annotation { "Feature Type Name" : "Feature", "Feature Type Description" : "" }
export const myFeature = defineFeature(function(context is Context, id is Id, definition is map)
    precondition{}
    {
        {
            var Q0;
            Q0=qCreatedBy(makeId("Front.planeOp"),FACE);
            var sketch = newSketch(context, id + "F0", { "sketchPlane" : qUnion([Q0])});
            skLineSegment(sketch, "E0.bottom", {"start": v(-30.04, 68.09) * mm, "end": v(46.16, 68.09) * mm});
            skLineSegment(sketch, "E0.top", {"start": v(-30.04, -46.79) * mm, "end": v(46.16, -46.79) * mm});
            skLineSegment(sketch, "E0.left", {"start": v(-30.04, 68.09) * mm, "end": v(-30.04, -46.79) * mm});
            skLineSegment(sketch, "E0.right", {"start": v(46.16, 68.09) * mm, "end": v(46.16, -46.79) * mm});
            skSolve(sketch);
        }
        {
            var Q0;
            Q0 = qSketchRegion(id + "F0", true);
            extrude(context, id + "F1", {"entities" : qUnion([Q0]), "depth" : 3.17 * mm});
        }
        {
            var Q0;
            Q0=makeQuery(id+"F1.opExtrude","CAP_FACE",FACE,{"disambiguationData":[OSD([sQuery(id+"F0.wireOp",EDGE,"E0.bottom"),sQuery(id+"F0.wireOp",EDGE,"E0.top"),sQuery(id+"F0.wireOp",EDGE,"E0.left"),sQuery(id+"F0.wireOp",EDGE,"E0.right")])],"isStart":false});
            var sketch = newSketch(context, id + "F2", { "sketchPlane" : qUnion([Q0])});
            skText(sketch, "E1", { "text": "STEM Academy", "fontName": "OpenSans-Regular.ttf"});
            skText(sketch, "E2", { "text": "Hall Pass", "fontName": "OpenSans-Regular.ttf"});
            skLineSegment(sketch, "E3", {"start": v(-8.97, 21.63) * mm, "end": v(2.74, 15.23) * mm});
            skLineSegment(sketch, "E4", {"start": v(2.74, 15.23) * mm, "end": v(10.3, 29.05) * mm});
            skLineSegment(sketch, "E5", {"start": v(-8.97, 21.63) * mm, "end": v(-4.91, 29.05) * mm});
            skLineSegment(sketch, "E6", {"start": v(15.54, 33.96) * mm, "end": v(1.33, 33.96) * mm});
            skArc(sketch, "E7", {"start": v(1.33, 33.96) * mm, "mid": v(-2.64, 32.58) * mm, "end": v(-4.91, 29.05) * mm});
            skArc(sketch, "E8", {"start": v(15.54, 33.96) * mm, "mid": v(12.52, 31.92) * mm, "end": v(10.3, 29.05) * mm});
            skLineSegment(sketch, "E9", {"start": v(11.32, 16.01) * mm, "end": v(23.65, 16.01) * mm});
            skLineSegment(sketch, "E10", {"start": v(23.65, 16.01) * mm, "end": v(28.78, 25.39) * mm});
            skLineSegment(sketch, "E11", {"start": v(28.78, 25.39) * mm, "end": v(25.68, 24.13) * mm});
            skLineSegment(sketch, "E12", {"start": v(11.32, 16.01) * mm, "end": v(14.76, 18.2) * mm});
            skLineSegment(sketch, "E13", {"start": v(14.76, 18.2) * mm, "end": v(10.23, 25.22) * mm});
            skLineSegment(sketch, "E14", {"start": v(25.68, 24.13) * mm, "end": v(21.62, 30.84) * mm});
            skArc(sketch, "E15", {"start": v(17.25, 32.24) * mm, "mid": v(12.84, 29.63) * mm, "end": v(10.23, 25.22) * mm});
            skArc(sketch, "E16", {"start": v(21.62, 30.84) * mm, "mid": v(19.7, 32.36) * mm, "end": v(17.25, 32.24) * mm});
            skLineSegment(sketch, "E17", {"start": v(-10.37, -1.78) * mm, "end": v(6.17, -1.78) * mm});
            skLineSegment(sketch, "E18", {"start": v(6.17, -1.78) * mm, "end": v(6.17, -14.73) * mm});
            skLineSegment(sketch, "E19", {"start": v(6.17, -14.73) * mm, "end": v(-3.97, -14.73) * mm});
            skLineSegment(sketch, "E20", {"start": v(-16.77, 0) * mm, "end": v(-9.6, -12.55) * mm});
            skArc(sketch, "E21", {"start": v(-16.77, 0) * mm, "mid": v(-13.94, -2.2) * mm, "end": v(-10.37, -1.78) * mm});
            skLineSegment(sketch, "E22", {"start": v(-17.39, 7.02) * mm, "end": v(-13.9, 13.97) * mm});
            skLineSegment(sketch, "E23", {"start": v(-13.9, 13.97) * mm, "end": v(-17.06, 16.57) * mm});
            skLineSegment(sketch, "E24", {"start": v(-17.06, 16.57) * mm, "end": v(-5.1, 16.57) * mm});
            skLineSegment(sketch, "E25", {"start": v(-5.1, 16.57) * mm, "end": v(0, 6.15) * mm});
            skLineSegment(sketch, "E26", {"start": v(0, 6.15) * mm, "end": v(-2.72, 7.56) * mm});
            skLineSegment(sketch, "E27", {"start": v(-2.72, 7.56) * mm, "end": v(-6.52, 0.5) * mm});
            skArc(sketch, "E28", {"start": v(-17.39, 7.02) * mm, "mid": v(-13.84, 0.62) * mm, "end": v(-6.52, 0.5) * mm});
            skLineSegment(sketch, "E29", {"start": v(28.67, -3.83) * mm, "end": v(20.63, 9.53) * mm});
            skLineSegment(sketch, "E30", {"start": v(20.63, 9.53) * mm, "end": v(31.4, 16.37) * mm});
            skLineSegment(sketch, "E31", {"start": v(31.4, 16.37) * mm, "end": v(37.58, 5.95) * mm});
            skLineSegment(sketch, "E32", {"start": v(37.36, 2.36) * mm, "end": v(30.19, -11) * mm});
            skLineSegment(sketch, "E33", {"start": v(25.41, -1.99) * mm, "end": v(17.48, -2.1) * mm});
            skLineSegment(sketch, "E34", {"start": v(17.48, -2.1) * mm, "end": v(17.16, 2.14) * mm});
            skLineSegment(sketch, "E35", {"start": v(17.16, 2.14) * mm, "end": v(10.74, -9.16) * mm});
            skLineSegment(sketch, "E36", {"start": v(10.74, -9.16) * mm, "end": v(16.93, -19.48) * mm});
            skLineSegment(sketch, "E37", {"start": v(16.93, -19.48) * mm, "end": v(17.15, -15.24) * mm});
            skLineSegment(sketch, "E38", {"start": v(17.15, -15.24) * mm, "end": v(26.28, -14.26) * mm});
            skArc(sketch, "E39", {"start": v(26.28, -14.26) * mm, "mid": v(28.67, -7.92) * mm, "end": v(25.41, -1.99) * mm});
            skArc(sketch, "E40", {"start": v(30.19, -11) * mm, "mid": v(30.03, -7.29) * mm, "end": v(28.67, -3.83) * mm});
            skArc(sketch, "E41", {"start": v(37.36, 2.36) * mm, "mid": v(37.86, 4.13) * mm, "end": v(37.58, 5.95) * mm});
            skArc(sketch, "E42", {"start": v(-9.6, -12.55) * mm, "mid": v(-7.1, -14.44) * mm, "end": v(-3.97, -14.73) * mm});
            skText(sketch, "E43", { "text": "Recycling", "fontName": "OpenSans-Regular.ttf"});
            skCircle(sketch, "E44", {"center": v(6.04, 63.9) * mm, "radius": 2.46 * mm});
            const initialGuessF2  = {"E1": [-0.01583, 0.04921, 1, 0, 0.00518], "E2": [-0.00708, 0.04127, 1, 0, 0.00576], "E43": [-0.02733, -0.03744, 1, 0, 0.01233]};
            skSetInitialGuess(sketch, initialGuessF2);
            skSolve(sketch);
        }
        {
            var Q0;
            Q0 = qSketchRegion(id + "F2", true);
            extrude(context, id + "F3", {"entities" : qUnion([Q0]), "operationType" : NewBodyOperationType.REMOVE, "oppositeDirection" : true, "depth" : 3.17 * mm});
        }
    });